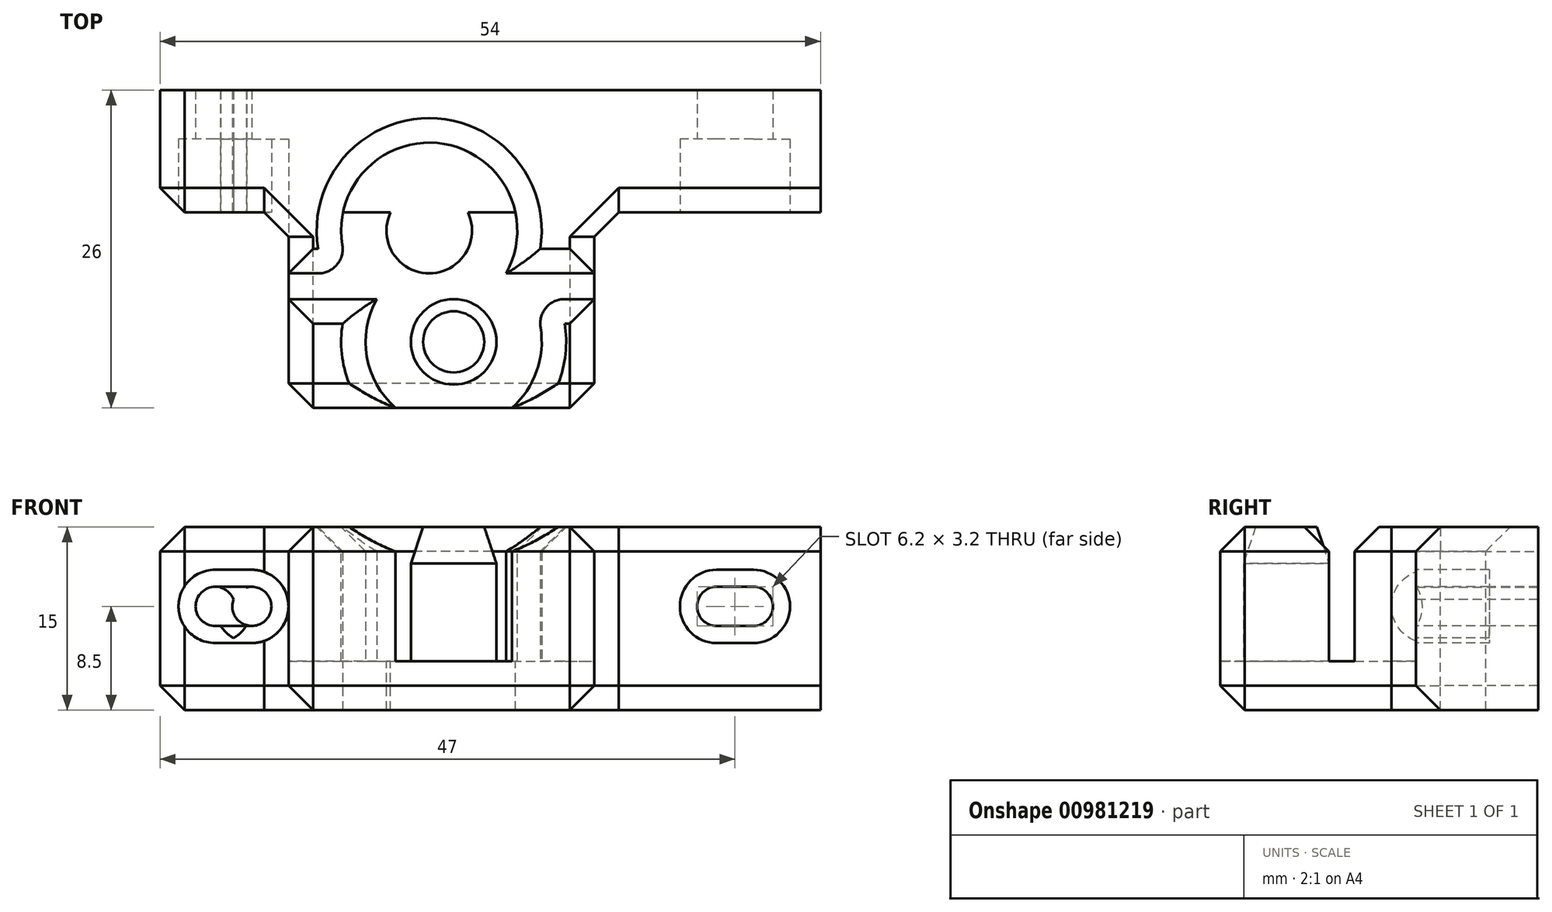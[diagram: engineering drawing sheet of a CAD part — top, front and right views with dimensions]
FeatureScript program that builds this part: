
annotation { "Feature Type Name" : "Feature", "Feature Type Description" : "" }
export const myFeature = defineFeature(function(context is Context, id is Id, definition is map)
    precondition{}
    {
        {
            var Q0;
            Q0=qCreatedBy(makeId("Top.planeOp"),FACE);
            var sketch = newSketch(context, id + "F0", { "sketchPlane" : qUnion([Q0])});
            skLineSegment(sketch, "E0.bottom", {"start": v(0, 0) * mm, "end": v(54, 0) * mm});
            skLineSegment(sketch, "E0.top", {"start": v(0, 10) * mm, "end": v(54, 10) * mm});
            skLineSegment(sketch, "E0.left", {"start": v(0, 0) * mm, "end": v(0, 10) * mm});
            skLineSegment(sketch, "E0.right", {"start": v(54, 0) * mm, "end": v(54, 10) * mm});
            skLineSegment(sketch, "E1.bottom", {"start": v(10.5, 0) * mm, "end": v(35.5, 0) * mm});
            skLineSegment(sketch, "E1.top", {"start": v(10.5, -16) * mm, "end": v(35.5, -16) * mm});
            skLineSegment(sketch, "E1.left", {"start": v(10.5, 0) * mm, "end": v(10.5, -16) * mm});
            skLineSegment(sketch, "E1.right", {"start": v(35.5, 0) * mm, "end": v(35.5, -16) * mm});
            skLineSegment(sketch, "E2", {"start": v(10.5, -5) * mm, "end": v(12.92, -5) * mm});
            skLineSegment(sketch, "E3", {"start": v(33.08, -7.1) * mm, "end": v(35.5, -7.1) * mm});
            skCircle(sketch, "E4", {"center": v(22, -1.5) * mm, "radius": 3.5 * mm});
            skCircle(sketch, "E5", {"center": v(24, -10.6) * mm, "radius": 3.5 * mm});
            skArc(sketch, "E6", {"start": v(28.76, -16) * mm, "mid": v(30.78, -13.02) * mm, "end": v(31.1, -9.43) * mm});
            skArc(sketch, "E7", {"start": v(28.3, -5) * mm, "mid": v(23.23, 5.6) * mm, "end": v(14.9, -2.67) * mm});
            skLineSegment(sketch, "E8", {"start": v(22, -1.5) * mm, "end": v(22, -19) * mm, "construction": true});
            skLineSegment(sketch, "E9", {"start": v(22, -19) * mm, "end": v(24, -19) * mm, "construction": true});
            skLineSegment(sketch, "E10", {"start": v(24, -19) * mm, "end": v(24, -10.6) * mm, "construction": true});
            skPoint(sketch, "E11", {"position": v(23, -16) * mm});
            skPoint(sketch, "E12", {"position": v(23, -19) * mm});
            skArc(sketch, "E13.trimOffspring", {"start": v(17.7, -7.1) * mm, "mid": v(16.9, -11.82) * mm, "end": v(19.24, -16) * mm});
            skPoint(sketch, "E14.newPointA", {"position": v(35.5, -5) * mm});
            skArc(sketch, "E14.filletArc", {"start": v(12.92, -5) * mm, "mid": v(14.45, -4.3) * mm, "end": v(14.9, -2.67) * mm});
            skArc(sketch, "E15.filletArc", {"start": v(33.08, -7.1) * mm, "mid": v(31.55, -7.8) * mm, "end": v(31.1, -9.43) * mm});
            skLineSegment(sketch, "E16", {"start": v(17.7, -7.1) * mm, "end": v(10.5, -7.1) * mm});
            skLineSegment(sketch, "E17", {"start": v(28.3, -5) * mm, "end": v(35.5, -5) * mm});
            skSolve(sketch);
        }
        {
            var Q0;
            Q0=makeQuery(id+"F0.imprint","IMPRINT",FACE,{"disambiguationData":[TD([[makeQuery(id+"F0.imprint","IMPRINT",EDGE,{"derivedFrom":sQuery(id+"F0.wireOp",EDGE,"E0.top")}),-1.0]])]});
            var Q1;
            {var subQ6=sQuery(id+"F0.wireOp",EDGE,"E2");Q1=makeQuery(id+"F0.imprint","IMPRINT",FACE,{"disambiguationData":[TD([[makeQuery(id+"F0.imprint","IMPRINT",EDGE,{"derivedFrom":subQ6}),1.0]])]});}
            var Q2;
            {var subQ3=sQuery(id+"F0.wireOp",EDGE,"E13.trimOffspring");Q2=makeQuery(id+"F0.imprint","IMPRINT",FACE,{"disambiguationData":[TD([[makeQuery(id+"F0.imprint","IMPRINT",EDGE,{"derivedFrom":subQ3}),-1.0]])]});}
            var Q3;
            {var subQ1=sQuery(id+"F0.wireOp",EDGE,"E3");Q3=makeQuery(id+"F0.imprint","IMPRINT",FACE,{"disambiguationData":[TD([[makeQuery(id+"F0.imprint","IMPRINT",EDGE,{"derivedFrom":subQ1}),-1.0]])]});}
            var Q4;
            {var subQ5=sQuery(id+"F0.wireOp",EDGE,"E17");Q4=makeQuery(id+"F0.imprint","IMPRINT",FACE,{"disambiguationData":[TD([[makeQuery(id+"F0.imprint","IMPRINT",EDGE,{"derivedFrom":subQ5}),1.0]])]});}
            var Q5;
            {var subQ13=sQuery(id+"F0.wireOp",EDGE,"E2");Q5=makeQuery(id+"F0.imprint","IMPRINT",FACE,{"disambiguationData":[TD([[makeQuery(id+"F0.imprint","IMPRINT",EDGE,{"derivedFrom":subQ13}),-1.0]])]});}
            var Q6;
            {var subQ0=sQuery(id+"F0.wireOp",EDGE,"E4");var subQ1=sQuery(id+"F0.wireOp",EDGE,"E1.bottom");var subQ2=makeQuery(id+"F0.imprint","INTERSECT",VERTEX,{"disambiguationData":[OD(0.0)],"derivedFrom":[subQ1,subQ0]});Q6=makeQuery(id+"F0.imprint","IMPRINT",FACE,{"disambiguationData":[TD([[makeQuery(id+"F0.imprint","IMPRINT",EDGE,{"disambiguationData":[TD([[subQ2,-1.0]])],"derivedFrom":subQ1}),-1.0]])]});}
            var Q7;
            Q7=makeQuery(id+"F0.imprint","IMPRINT",FACE,{"disambiguationData":[TD([[makeQuery(id+"F0.imprint","IMPRINT",EDGE,{"derivedFrom":sQuery(id+"F0.wireOp",EDGE,"E5")}),1.0]])]});
            var Q8;
            {var subQ0=sQuery(id+"F0.wireOp",EDGE,"E4");var subQ1=sQuery(id+"F0.wireOp",EDGE,"E1.bottom");var subQ2=makeQuery(id+"F0.imprint","INTERSECT",VERTEX,{"disambiguationData":[OD(0.0)],"derivedFrom":[subQ1,subQ0]});Q8=makeQuery(id+"F0.imprint","IMPRINT",FACE,{"disambiguationData":[TD([[makeQuery(id+"F0.imprint","IMPRINT",EDGE,{"disambiguationData":[TD([[subQ2,-1.0]])],"derivedFrom":subQ1}),1.0]])]});}
            var Q9;
            {var subQ0=sQuery(id+"F0.wireOp",EDGE,"E7");var subQ1=sQuery(id+"F0.wireOp",EDGE,"E1.bottom");var subQ2=makeQuery(id+"F0.imprint","INTERSECT",VERTEX,{"disambiguationData":[OD(0.0)],"derivedFrom":[subQ1,subQ0]});Q9=makeQuery(id+"F0.imprint","IMPRINT",FACE,{"disambiguationData":[TD([[makeQuery(id+"F0.imprint","IMPRINT",EDGE,{"disambiguationData":[TD([[subQ2,-1.0]])],"derivedFrom":subQ1}),1.0]])]});}
            extrude(context, id + "F1", {"entities" : qUnion([Q0, Q1, Q2, Q3, Q4, Q5, Q6, Q7, Q8, Q9]), "oppositeDirection" : true, "depth" : 4 * mm, "offsetDistance" : 25 * mm});
        }
        {
            var Q0;
            Q0=makeQuery(id+"F0.imprint","IMPRINT",FACE,{"disambiguationData":[TD([[makeQuery(id+"F0.imprint","IMPRINT",EDGE,{"derivedFrom":sQuery(id+"F0.wireOp",EDGE,"E0.top")}),-1.0]])]});
            var Q1;
            {var subQ5=sQuery(id+"F0.wireOp",EDGE,"E17");Q1=makeQuery(id+"F0.imprint","IMPRINT",FACE,{"disambiguationData":[TD([[makeQuery(id+"F0.imprint","IMPRINT",EDGE,{"derivedFrom":subQ5}),1.0]])]});}
            var Q2;
            {var subQ6=sQuery(id+"F0.wireOp",EDGE,"E2");Q2=makeQuery(id+"F0.imprint","IMPRINT",FACE,{"disambiguationData":[TD([[makeQuery(id+"F0.imprint","IMPRINT",EDGE,{"derivedFrom":subQ6}),1.0]])]});}
            var Q3;
            {var subQ3=sQuery(id+"F0.wireOp",EDGE,"E13.trimOffspring");Q3=makeQuery(id+"F0.imprint","IMPRINT",FACE,{"disambiguationData":[TD([[makeQuery(id+"F0.imprint","IMPRINT",EDGE,{"derivedFrom":subQ3}),-1.0]])]});}
            var Q4;
            {var subQ1=sQuery(id+"F0.wireOp",EDGE,"E3");Q4=makeQuery(id+"F0.imprint","IMPRINT",FACE,{"disambiguationData":[TD([[makeQuery(id+"F0.imprint","IMPRINT",EDGE,{"derivedFrom":subQ1}),-1.0]])]});}
            var Q5;
            Q5=makeQuery(id+"F0.imprint","IMPRINT",FACE,{"disambiguationData":[TD([[makeQuery(id+"F0.imprint","IMPRINT",EDGE,{"derivedFrom":sQuery(id+"F0.wireOp",EDGE,"E5")}),1.0]])]});
            var Q6;
            {var subQ0=sQuery(id+"F0.wireOp",EDGE,"E4");var subQ1=sQuery(id+"F0.wireOp",EDGE,"E1.bottom");var subQ2=makeQuery(id+"F0.imprint","INTERSECT",VERTEX,{"disambiguationData":[OD(0.0)],"derivedFrom":[subQ1,subQ0]});Q6=makeQuery(id+"F0.imprint","IMPRINT",FACE,{"disambiguationData":[TD([[makeQuery(id+"F0.imprint","IMPRINT",EDGE,{"disambiguationData":[TD([[subQ2,-1.0]])],"derivedFrom":subQ1}),-1.0]])]});}
            var Q7;
            {var subQ0=sQuery(id+"F0.wireOp",EDGE,"E4");var subQ1=sQuery(id+"F0.wireOp",EDGE,"E1.bottom");var subQ2=makeQuery(id+"F0.imprint","INTERSECT",VERTEX,{"disambiguationData":[OD(0.0)],"derivedFrom":[subQ1,subQ0]});Q7=makeQuery(id+"F0.imprint","IMPRINT",FACE,{"disambiguationData":[TD([[makeQuery(id+"F0.imprint","IMPRINT",EDGE,{"disambiguationData":[TD([[subQ2,-1.0]])],"derivedFrom":subQ1}),1.0]])]});}
            extrude(context, id + "F2", {"entities" : qUnion([Q0, Q1, Q2, Q3, Q4, Q5, Q6, Q7]), "operationType" : NewBodyOperationType.ADD, "depth" : 11 * mm, "offsetDistance" : 25 * mm});
        }
        {
            var Q0;
            Q0=makeQuery(id+"F2.opExtrude","CAP_EDGE",EDGE,{"disambiguationData":[OSD([sQuery(id+"F0.wireOp",EDGE,"E2")])],"isStart":false});
            var Q1;
            Q1=makeQuery(id+"F2.opExtrude","CAP_EDGE",EDGE,{"disambiguationData":[OSD([sQuery(id+"F0.wireOp",EDGE,"E17")])],"isStart":false});
            var Q2;
            Q2=makeQuery(id+"F2.opExtrude","CAP_EDGE",EDGE,{"disambiguationData":[OSD([sQuery(id+"F0.wireOp",EDGE,"E3")])],"isStart":false});
            var Q3;
            Q3=makeQuery(id+"F2.opExtrude","CAP_EDGE",EDGE,{"disambiguationData":[OSD([sQuery(id+"F0.wireOp",EDGE,"E13.trimOffspring")])],"isStart":false});
            var Q4;
            Q4=makeQuery(id+"F2.opExtrude","CAP_EDGE",EDGE,{"disambiguationData":[OSD([sQuery(id+"F0.wireOp",EDGE,"E16")])],"isStart":false});
            chamfer(context, id + "F3", {"entities" : qUnion([Q0, Q1, Q2, Q3, Q4]), "width" : 2 * mm, "tangentPropagation" : true});
        }
        {
            var Q0;
            Q0=makeQuery(id+"F2.opExtrude","CAP_FACE",FACE,{"disambiguationData":[OSD([sQuery(id+"F0.wireOp",EDGE,"E4")])],"isStart":false});
            var Q1;
            Q1=makeQuery(id+"F2.opExtrude","CAP_EDGE",EDGE,{"disambiguationData":[OSD([sQuery(id+"F0.wireOp",EDGE,"E5")])],"isStart":false});
            chamfer(context, id + "F4", {"entities" : qUnion([Q0, Q1]), "chamferType" : ChamferType.TWO_OFFSETS, "width1" : 1 * mm, "oppositeDirection" : false, "width2" : 3 * mm, "tangentPropagation" : true});
        }
        {
            var Q0;
            {var subQ0=sQuery(id+"F0.wireOp",EDGE,"E0.bottom");var subQ1=makeQuery(id+"F0.imprint","IMPRINT",EDGE,{"disambiguationData":[TD([[makeQuery(id+"F0.imprint","INTERSECT",VERTEX,{"derivedFrom":[subQ0,sQuery(id+"F0.wireOp",EDGE,"E0.right")]}),1.0]])],"derivedFrom":subQ0});Q0=makeQuery(id+"F2.boolean.opBoolean","MERGE",FACE,{"derivedFrom":[makeQuery(id+"F1.opExtrude","SWEPT_FACE",FACE,{"disambiguationData":[OSD([subQ0]),TDD([subQ1])]}),makeQuery(id+"F2.opExtrude","SWEPT_FACE",FACE,{"disambiguationData":[OSD([subQ0]),TDD([subQ1])]})]});}
            var sketch = newSketch(context, id + "F5", { "sketchPlane" : qUnion([Q0])});
            skCircle(sketch, "E18", {"center": v(4.5, 4.5) * mm, "radius": 1.6 * mm});
            skCircle(sketch, "E19", {"center": v(4.5, 4.5) * mm, "radius": 3 * mm});
            skCircle(sketch, "E20", {"center": v(48.5, 4.5) * mm, "radius": 1.6 * mm});
            skCircle(sketch, "E21", {"center": v(48.5, 4.5) * mm, "radius": 3 * mm});
            skCircle(sketch, "E22", {"center": v(7.5, 4.5) * mm, "radius": 1.6 * mm});
            skCircle(sketch, "E23", {"center": v(7.5, 4.5) * mm, "radius": 3 * mm});
            skCircle(sketch, "E24", {"center": v(45.5, 4.5) * mm, "radius": 1.6 * mm});
            skCircle(sketch, "E25", {"center": v(45.5, 4.5) * mm, "radius": 3 * mm});
            skLineSegment(sketch, "E26", {"start": v(4.5, 6.1) * mm, "end": v(7.5, 6.1) * mm});
            skLineSegment(sketch, "E27", {"start": v(7.5, 2.9) * mm, "end": v(4.5, 2.9) * mm});
            skLineSegment(sketch, "E28", {"start": v(45.5, 2.9) * mm, "end": v(48.5, 2.9) * mm});
            skLineSegment(sketch, "E29", {"start": v(48.5, 6.1) * mm, "end": v(45.5, 6.1) * mm});
            skLineSegment(sketch, "E30", {"start": v(45.5, 7.5) * mm, "end": v(48.5, 7.5) * mm});
            skLineSegment(sketch, "E31", {"start": v(48.5, 1.5) * mm, "end": v(45.5, 1.5) * mm});
            skLineSegment(sketch, "E32", {"start": v(7.5, 7.5) * mm, "end": v(4.5, 7.5) * mm});
            skLineSegment(sketch, "E33", {"start": v(4.5, 1.5) * mm, "end": v(7.5, 1.5) * mm});
            skSolve(sketch);
        }
        {
            var Q0;
            {var subQ0=sQuery(id+"F5.wireOp",EDGE,"E18");var subQ1=makeQuery(id+"F5.imprint","INTERSECT",VERTEX,{"derivedFrom":[subQ0,sQuery(id+"F5.wireOp",EDGE,"E26")]});Q0=makeQuery(id+"F5.imprint","IMPRINT",FACE,{"disambiguationData":[TD([[makeQuery(id+"F5.imprint","IMPRINT",EDGE,{"disambiguationData":[TD([[subQ1,1.0]])],"derivedFrom":subQ0}),1.0]])]});}
            var Q1;
            {var subQ0=sQuery(id+"F5.wireOp",EDGE,"E23");var subQ1=sQuery(id+"F5.wireOp",EDGE,"E18");var subQ2=makeQuery(id+"F5.imprint","INTERSECT",VERTEX,{"disambiguationData":[OD(0.0)],"derivedFrom":[subQ1,subQ0]});Q1=makeQuery(id+"F5.imprint","IMPRINT",FACE,{"disambiguationData":[TD([[makeQuery(id+"F5.imprint","IMPRINT",EDGE,{"disambiguationData":[TD([[subQ2,1.0]])],"derivedFrom":subQ1}),1.0]])]});}
            var Q2;
            {var subQ0=sQuery(id+"F5.wireOp",EDGE,"E22");var subQ1=sQuery(id+"F5.wireOp",EDGE,"E18");var subQ2=makeQuery(id+"F5.imprint","INTERSECT",VERTEX,{"disambiguationData":[OD(0.0)],"derivedFrom":[subQ1,subQ0]});Q2=makeQuery(id+"F5.imprint","IMPRINT",FACE,{"disambiguationData":[TD([[makeQuery(id+"F5.imprint","IMPRINT",EDGE,{"disambiguationData":[TD([[subQ2,1.0]])],"derivedFrom":subQ1}),-1.0]])]});}
            var Q3;
            {var subQ1=sQuery(id+"F5.wireOp",EDGE,"E18");var subQ5=sQuery(id+"F5.wireOp",EDGE,"E23");var subQ6=makeQuery(id+"F5.imprint","INTERSECT",VERTEX,{"disambiguationData":[OD(0.0)],"derivedFrom":[subQ1,subQ5]});Q3=makeQuery(id+"F5.imprint","IMPRINT",FACE,{"disambiguationData":[TD([[makeQuery(id+"F5.imprint","IMPRINT",EDGE,{"disambiguationData":[TD([[subQ6,1.0]])],"derivedFrom":subQ1}),-1.0]])]});}
            var Q4;
            {var subQ0=sQuery(id+"F5.wireOp",EDGE,"E22");var subQ1=sQuery(id+"F5.wireOp",EDGE,"E18");var subQ2=makeQuery(id+"F5.imprint","INTERSECT",VERTEX,{"disambiguationData":[OD(0.0)],"derivedFrom":[subQ1,subQ0]});Q4=makeQuery(id+"F5.imprint","IMPRINT",FACE,{"disambiguationData":[TD([[makeQuery(id+"F5.imprint","IMPRINT",EDGE,{"disambiguationData":[TD([[subQ2,1.0]])],"derivedFrom":subQ1}),1.0]])]});}
            var Q5;
            {var subQ0=sQuery(id+"F5.wireOp",EDGE,"E23");var subQ1=sQuery(id+"F5.wireOp",EDGE,"E18");var subQ2=makeQuery(id+"F5.imprint","INTERSECT",VERTEX,{"disambiguationData":[OD(1.0)],"derivedFrom":[subQ1,subQ0]});Q5=makeQuery(id+"F5.imprint","IMPRINT",FACE,{"disambiguationData":[TD([[makeQuery(id+"F5.imprint","IMPRINT",EDGE,{"disambiguationData":[TD([[subQ2,-1.0]])],"derivedFrom":subQ1}),-1.0]])]});}
            var Q6;
            {var subQ0=sQuery(id+"F5.wireOp",EDGE,"E22");var subQ1=sQuery(id+"F5.wireOp",EDGE,"E19");var subQ2=makeQuery(id+"F5.imprint","INTERSECT",VERTEX,{"disambiguationData":[OD(0.0)],"derivedFrom":[subQ1,subQ0]});Q6=makeQuery(id+"F5.imprint","IMPRINT",FACE,{"disambiguationData":[TD([[makeQuery(id+"F5.imprint","IMPRINT",EDGE,{"disambiguationData":[TD([[subQ2,1.0]])],"derivedFrom":subQ1}),-1.0]])]});}
            var Q7;
            {var subQ0=sQuery(id+"F5.wireOp",EDGE,"E27");var subQ1=sQuery(id+"F5.wireOp",EDGE,"E19");var subQ2=makeQuery(id+"F5.imprint","INTERSECT",VERTEX,{"derivedFrom":[subQ1,subQ0]});Q7=makeQuery(id+"F5.imprint","IMPRINT",FACE,{"disambiguationData":[TD([[makeQuery(id+"F5.imprint","IMPRINT",EDGE,{"disambiguationData":[TD([[subQ2,-1.0]])],"derivedFrom":subQ1}),-1.0]])]});}
            var Q8;
            {var subQ0=sQuery(id+"F5.wireOp",EDGE,"E27");var subQ1=sQuery(id+"F5.wireOp",EDGE,"E18");var subQ2=makeQuery(id+"F5.imprint","INTERSECT",VERTEX,{"derivedFrom":[subQ1,subQ0]});Q8=makeQuery(id+"F5.imprint","IMPRINT",FACE,{"disambiguationData":[TD([[makeQuery(id+"F5.imprint","IMPRINT",EDGE,{"disambiguationData":[TD([[subQ2,-1.0]])],"derivedFrom":subQ1}),-1.0]])]});}
            var Q9;
            {var subQ0=sQuery(id+"F5.wireOp",EDGE,"E26");var subQ1=sQuery(id+"F5.wireOp",EDGE,"E18");var subQ2=makeQuery(id+"F5.imprint","INTERSECT",VERTEX,{"derivedFrom":[subQ1,subQ0]});Q9=makeQuery(id+"F5.imprint","IMPRINT",FACE,{"disambiguationData":[TD([[makeQuery(id+"F5.imprint","IMPRINT",EDGE,{"disambiguationData":[TD([[subQ2,1.0]])],"derivedFrom":subQ1}),-1.0]])]});}
            var Q10;
            {var subQ0=sQuery(id+"F5.wireOp",EDGE,"E26");var subQ1=sQuery(id+"F5.wireOp",EDGE,"E19");var subQ2=makeQuery(id+"F5.imprint","INTERSECT",VERTEX,{"derivedFrom":[subQ1,subQ0]});Q10=makeQuery(id+"F5.imprint","IMPRINT",FACE,{"disambiguationData":[TD([[makeQuery(id+"F5.imprint","IMPRINT",EDGE,{"disambiguationData":[TD([[subQ2,1.0]])],"derivedFrom":subQ1}),-1.0]])]});}
            var Q11;
            {var subQ0=sQuery(id+"F5.wireOp",EDGE,"E24");var subQ1=sQuery(id+"F5.wireOp",EDGE,"E20");var subQ2=makeQuery(id+"F5.imprint","INTERSECT",VERTEX,{"disambiguationData":[OD(0.0)],"derivedFrom":[subQ1,subQ0]});Q11=makeQuery(id+"F5.imprint","IMPRINT",FACE,{"disambiguationData":[TD([[makeQuery(id+"F5.imprint","IMPRINT",EDGE,{"disambiguationData":[TD([[subQ2,-1.0]])],"derivedFrom":subQ1}),1.0]])]});}
            var Q12;
            {var subQ0=sQuery(id+"F5.wireOp",EDGE,"E25");var subQ1=sQuery(id+"F5.wireOp",EDGE,"E20");var subQ2=makeQuery(id+"F5.imprint","INTERSECT",VERTEX,{"disambiguationData":[OD(0.0)],"derivedFrom":[subQ1,subQ0]});Q12=makeQuery(id+"F5.imprint","IMPRINT",FACE,{"disambiguationData":[TD([[makeQuery(id+"F5.imprint","IMPRINT",EDGE,{"disambiguationData":[TD([[subQ2,-1.0]])],"derivedFrom":subQ1}),1.0]])]});}
            var Q13;
            {var subQ0=sQuery(id+"F5.wireOp",EDGE,"E25");var subQ1=sQuery(id+"F5.wireOp",EDGE,"E20");var subQ2=makeQuery(id+"F5.imprint","INTERSECT",VERTEX,{"disambiguationData":[OD(0.0)],"derivedFrom":[subQ1,subQ0]});Q13=makeQuery(id+"F5.imprint","IMPRINT",FACE,{"disambiguationData":[TD([[makeQuery(id+"F5.imprint","IMPRINT",EDGE,{"disambiguationData":[TD([[subQ2,-1.0]])],"derivedFrom":subQ1}),-1.0]])]});}
            var Q14;
            {var subQ0=sQuery(id+"F5.wireOp",EDGE,"E24");var subQ1=sQuery(id+"F5.wireOp",EDGE,"E20");var subQ2=makeQuery(id+"F5.imprint","INTERSECT",VERTEX,{"disambiguationData":[OD(0.0)],"derivedFrom":[subQ1,subQ0]});Q14=makeQuery(id+"F5.imprint","IMPRINT",FACE,{"disambiguationData":[TD([[makeQuery(id+"F5.imprint","IMPRINT",EDGE,{"disambiguationData":[TD([[subQ2,-1.0]])],"derivedFrom":subQ1}),-1.0]])]});}
            var Q15;
            {var subQ0=sQuery(id+"F5.wireOp",EDGE,"E24");var subQ1=sQuery(id+"F5.wireOp",EDGE,"E20");var subQ2=makeQuery(id+"F5.imprint","INTERSECT",VERTEX,{"disambiguationData":[OD(1.0)],"derivedFrom":[subQ1,subQ0]});Q15=makeQuery(id+"F5.imprint","IMPRINT",FACE,{"disambiguationData":[TD([[makeQuery(id+"F5.imprint","IMPRINT",EDGE,{"disambiguationData":[TD([[subQ2,-1.0]])],"derivedFrom":subQ1}),-1.0]])]});}
            var Q16;
            {var subQ0=sQuery(id+"F5.wireOp",EDGE,"E24");var subQ1=sQuery(id+"F5.wireOp",EDGE,"E21");var subQ2=makeQuery(id+"F5.imprint","INTERSECT",VERTEX,{"disambiguationData":[OD(0.0)],"derivedFrom":[subQ1,subQ0]});Q16=makeQuery(id+"F5.imprint","IMPRINT",FACE,{"disambiguationData":[TD([[makeQuery(id+"F5.imprint","IMPRINT",EDGE,{"disambiguationData":[TD([[subQ2,-1.0]])],"derivedFrom":subQ1}),-1.0]])]});}
            var Q17;
            {var subQ0=sQuery(id+"F5.wireOp",EDGE,"E20");var subQ1=makeQuery(id+"F5.imprint","INTERSECT",VERTEX,{"derivedFrom":[subQ0,sQuery(id+"F5.wireOp",EDGE,"E29")]});Q17=makeQuery(id+"F5.imprint","IMPRINT",FACE,{"disambiguationData":[TD([[makeQuery(id+"F5.imprint","IMPRINT",EDGE,{"disambiguationData":[TD([[subQ1,-1.0]])],"derivedFrom":subQ0}),1.0]])]});}
            var Q18;
            {var subQ0=sQuery(id+"F5.wireOp",EDGE,"E28");var subQ1=sQuery(id+"F5.wireOp",EDGE,"E20");var subQ2=makeQuery(id+"F5.imprint","INTERSECT",VERTEX,{"derivedFrom":[subQ1,subQ0]});Q18=makeQuery(id+"F5.imprint","IMPRINT",FACE,{"disambiguationData":[TD([[makeQuery(id+"F5.imprint","IMPRINT",EDGE,{"disambiguationData":[TD([[subQ2,1.0]])],"derivedFrom":subQ1}),-1.0]])]});}
            var Q19;
            {var subQ0=sQuery(id+"F5.wireOp",EDGE,"E24");var subQ1=sQuery(id+"F5.wireOp",EDGE,"E21");var subQ2=makeQuery(id+"F5.imprint","INTERSECT",VERTEX,{"disambiguationData":[OD(1.0)],"derivedFrom":[subQ1,subQ0]});Q19=makeQuery(id+"F5.imprint","IMPRINT",FACE,{"disambiguationData":[TD([[makeQuery(id+"F5.imprint","IMPRINT",EDGE,{"disambiguationData":[TD([[subQ2,-1.0]])],"derivedFrom":subQ1}),-1.0]])]});}
            var Q20;
            {var subQ0=sQuery(id+"F5.wireOp",EDGE,"E29");var subQ1=sQuery(id+"F5.wireOp",EDGE,"E21");var subQ2=makeQuery(id+"F5.imprint","INTERSECT",VERTEX,{"derivedFrom":[subQ1,subQ0]});Q20=makeQuery(id+"F5.imprint","IMPRINT",FACE,{"disambiguationData":[TD([[makeQuery(id+"F5.imprint","IMPRINT",EDGE,{"disambiguationData":[TD([[subQ2,-1.0]])],"derivedFrom":subQ1}),-1.0]])]});}
            var Q21;
            {var subQ0=sQuery(id+"F5.wireOp",EDGE,"E29");var subQ1=sQuery(id+"F5.wireOp",EDGE,"E20");var subQ2=makeQuery(id+"F5.imprint","INTERSECT",VERTEX,{"derivedFrom":[subQ1,subQ0]});Q21=makeQuery(id+"F5.imprint","IMPRINT",FACE,{"disambiguationData":[TD([[makeQuery(id+"F5.imprint","IMPRINT",EDGE,{"disambiguationData":[TD([[subQ2,-1.0]])],"derivedFrom":subQ1}),-1.0]])]});}
            extrude(context, id + "F6", {"entities" : qUnion([Q0, Q1, Q2, Q3, Q4, Q5, Q6, Q7, Q8, Q9, Q10, Q11, Q12, Q13, Q14, Q15, Q16, Q17, Q18, Q19, Q20, Q21]), "operationType" : NewBodyOperationType.REMOVE, "endBound" : BoundingType.THROUGH_ALL, "oppositeDirection" : true, "depth" : 25 * mm, "offsetDistance" : 25 * mm});
        }
        {
            var Q0;
            {var subQ6=sQuery(id+"F5.wireOp",EDGE,"E26");var subQ7=sQuery(id+"F5.wireOp",EDGE,"E18");var subQ8=makeQuery(id+"F5.imprint","INTERSECT",VERTEX,{"derivedFrom":[subQ7,subQ6]});Q0=makeQuery(id+"F5.imprint","IMPRINT",FACE,{"disambiguationData":[TD([[makeQuery(id+"F5.imprint","IMPRINT",EDGE,{"disambiguationData":[TD([[subQ8,-1.0]])],"derivedFrom":subQ7}),-1.0]])]});}
            var Q1;
            {var subQ2=sQuery(id+"F5.wireOp",EDGE,"E19");var subQ4=sQuery(id+"F5.wireOp",EDGE,"E26");var subQ11=makeQuery(id+"F5.imprint","INTERSECT",VERTEX,{"derivedFrom":[subQ2,subQ4]});Q1=makeQuery(id+"F5.imprint","IMPRINT",FACE,{"disambiguationData":[TD([[makeQuery(id+"F5.imprint","IMPRINT",EDGE,{"disambiguationData":[TD([[subQ11,-1.0]])],"derivedFrom":subQ2}),-1.0]])]});}
            var Q2;
            {var subQ0=sQuery(id+"F5.wireOp",EDGE,"E26");var subQ1=sQuery(id+"F5.wireOp",EDGE,"E19");var subQ2=makeQuery(id+"F5.imprint","INTERSECT",VERTEX,{"derivedFrom":[subQ1,subQ0]});Q2=makeQuery(id+"F5.imprint","IMPRINT",FACE,{"disambiguationData":[TD([[makeQuery(id+"F5.imprint","IMPRINT",EDGE,{"disambiguationData":[TD([[subQ2,-1.0]])],"derivedFrom":subQ1}),1.0]])]});}
            var Q3;
            {var subQ0=sQuery(id+"F5.wireOp",EDGE,"E23");var subQ1=sQuery(id+"F5.wireOp",EDGE,"E19");var subQ2=makeQuery(id+"F5.imprint","INTERSECT",VERTEX,{"disambiguationData":[OD(1.0)],"derivedFrom":[subQ1,subQ0]});Q3=makeQuery(id+"F5.imprint","IMPRINT",FACE,{"disambiguationData":[TD([[makeQuery(id+"F5.imprint","IMPRINT",EDGE,{"disambiguationData":[TD([[subQ2,-1.0]])],"derivedFrom":subQ1}),1.0]])]});}
            var Q4;
            {var subQ0=sQuery(id+"F5.wireOp",EDGE,"E33");Q4=makeQuery(id+"F5.imprint","IMPRINT",FACE,{"disambiguationData":[TD([[makeQuery(id+"F5.imprint","IMPRINT",EDGE,{"derivedFrom":subQ0}),1.0]])]});}
            var Q5;
            {var subQ0=sQuery(id+"F5.wireOp",EDGE,"E32");Q5=makeQuery(id+"F5.imprint","IMPRINT",FACE,{"disambiguationData":[TD([[makeQuery(id+"F5.imprint","IMPRINT",EDGE,{"derivedFrom":subQ0}),1.0]])]});}
            var Q6;
            {var subQ0=sQuery(id+"F5.wireOp",EDGE,"E28");var subQ1=sQuery(id+"F5.wireOp",EDGE,"E21");var subQ2=makeQuery(id+"F5.imprint","INTERSECT",VERTEX,{"derivedFrom":[subQ1,subQ0]});Q6=makeQuery(id+"F5.imprint","IMPRINT",FACE,{"disambiguationData":[TD([[makeQuery(id+"F5.imprint","IMPRINT",EDGE,{"disambiguationData":[TD([[subQ2,-1.0]])],"derivedFrom":subQ1}),1.0]])]});}
            var Q7;
            {var subQ0=sQuery(id+"F5.wireOp",EDGE,"E25");var subQ1=sQuery(id+"F5.wireOp",EDGE,"E21");var subQ2=makeQuery(id+"F5.imprint","INTERSECT",VERTEX,{"disambiguationData":[OD(0.0)],"derivedFrom":[subQ1,subQ0]});Q7=makeQuery(id+"F5.imprint","IMPRINT",FACE,{"disambiguationData":[TD([[makeQuery(id+"F5.imprint","IMPRINT",EDGE,{"disambiguationData":[TD([[subQ2,-1.0]])],"derivedFrom":subQ1}),1.0]])]});}
            var Q8;
            {var subQ0=sQuery(id+"F5.wireOp",EDGE,"E30");Q8=makeQuery(id+"F5.imprint","IMPRINT",FACE,{"disambiguationData":[TD([[makeQuery(id+"F5.imprint","IMPRINT",EDGE,{"derivedFrom":subQ0}),-1.0]])]});}
            var Q9;
            {var subQ0=sQuery(id+"F5.wireOp",EDGE,"E31");Q9=makeQuery(id+"F5.imprint","IMPRINT",FACE,{"disambiguationData":[TD([[makeQuery(id+"F5.imprint","IMPRINT",EDGE,{"derivedFrom":subQ0}),-1.0]])]});}
            var Q10;
            {var subQ8=sQuery(id+"F5.wireOp",EDGE,"E28");var subQ10=sQuery(id+"F5.wireOp",EDGE,"E20");var subQ11=makeQuery(id+"F5.imprint","INTERSECT",VERTEX,{"derivedFrom":[subQ10,subQ8]});Q10=makeQuery(id+"F5.imprint","IMPRINT",FACE,{"disambiguationData":[TD([[makeQuery(id+"F5.imprint","IMPRINT",EDGE,{"disambiguationData":[TD([[subQ11,-1.0]])],"derivedFrom":subQ10}),-1.0]])]});}
            var Q11;
            {var subQ5=sQuery(id+"F5.wireOp",EDGE,"E25");var subQ7=sQuery(id+"F5.wireOp",EDGE,"E21");var subQ8=makeQuery(id+"F5.imprint","INTERSECT",VERTEX,{"disambiguationData":[OD(0.0)],"derivedFrom":[subQ7,subQ5]});Q11=makeQuery(id+"F5.imprint","IMPRINT",FACE,{"disambiguationData":[TD([[makeQuery(id+"F5.imprint","IMPRINT",EDGE,{"disambiguationData":[TD([[subQ8,-1.0]])],"derivedFrom":subQ7}),-1.0]])]});}
            extrude(context, id + "F7", {"entities" : qUnion([Q0, Q1, Q2, Q3, Q4, Q5, Q6, Q7, Q8, Q9, Q10, Q11]), "operationType" : NewBodyOperationType.REMOVE, "oppositeDirection" : true, "depth" : 6 * mm, "offsetDistance" : 25 * mm});
        }
        {
            var Q0;
            {var subQ0=sQuery(id+"F0.wireOp",EDGE,"E1.left");var subQ1=sQuery(id+"F0.wireOp",EDGE,"E1.top");Q0=makeQuery(id+"F2.boolean.opBoolean","MERGE",EDGE,{"derivedFrom":[makeQuery(id+"F1.opExtrude","SWEPT_EDGE",EDGE,{"disambiguationData":[OSD([subQ1,subQ0])]}),makeQuery(id+"F2.opExtrude","SWEPT_EDGE",EDGE,{"disambiguationData":[OSD([subQ1,subQ0])]})]});}
            var Q1;
            {var subQ0=sQuery(id+"F0.wireOp",EDGE,"E1.right");var subQ1=sQuery(id+"F0.wireOp",EDGE,"E1.top");Q1=makeQuery(id+"F2.boolean.opBoolean","MERGE",EDGE,{"derivedFrom":[makeQuery(id+"F1.opExtrude","SWEPT_EDGE",EDGE,{"disambiguationData":[OSD([subQ1,subQ0])]}),makeQuery(id+"F2.opExtrude","SWEPT_EDGE",EDGE,{"disambiguationData":[OSD([subQ1,subQ0])]})]});}
            var Q2;
            {var subQ0=sQuery(id+"F0.wireOp",EDGE,"E1.right");var subQ1=sQuery(id+"F0.wireOp",EDGE,"E1.bottom");var subQ2=sQuery(id+"F0.wireOp",EDGE,"E0.bottom");Q2=makeQuery(id+"F2.boolean.opBoolean","MERGE",EDGE,{"derivedFrom":[makeQuery(id+"F1.opExtrude","SWEPT_EDGE",EDGE,{"disambiguationData":[OSD([subQ2,subQ1,subQ0])]}),makeQuery(id+"F2.opExtrude","SWEPT_EDGE",EDGE,{"disambiguationData":[OSD([subQ2,subQ1,subQ0])]})]});}
            var Q3;
            {var subQ0=sQuery(id+"F0.wireOp",EDGE,"E0.left");var subQ1=sQuery(id+"F0.wireOp",EDGE,"E0.bottom");var subQ2=sQuery(id+"F0.wireOp",EDGE,"E1.left");var subQ3=sQuery(id+"F0.wireOp",EDGE,"E1.bottom");var subQ6=sQuery(id+"F0.wireOp",EDGE,"E2");Q3=makeQuery(id+"F7.boolean.opBoolean","SPLIT",EDGE,{"disambiguationData":[TD([makeQuery(id+"F2.opExtrude","CAP_FACE",FACE,{"disambiguationData":[OSD([subQ1,sQuery(id+"F0.wireOp",EDGE,"E0.top"),subQ0,sQuery(id+"F0.wireOp",EDGE,"E0.right"),subQ2,sQuery(id+"F0.wireOp",EDGE,"E1.right"),subQ6,sQuery(id+"F0.wireOp",EDGE,"E7"),sQuery(id+"F0.wireOp",EDGE,"E14.filletArc"),sQuery(id+"F0.wireOp",EDGE,"E17")])],"isStart":false})])],"derivedFrom":makeQuery(id+"F2.boolean.opBoolean","MERGE",EDGE,{"derivedFrom":[makeQuery(id+"F1.opExtrude","SWEPT_EDGE",EDGE,{"disambiguationData":[OSD([subQ1,subQ3,subQ2])]}),makeQuery(id+"F2.opExtrude","SWEPT_EDGE",EDGE,{"disambiguationData":[OSD([subQ1,subQ3,subQ2])]})]})});}
            var Q4;
            {var subQ0=sQuery(id+"F0.wireOp",EDGE,"E0.left");var subQ1=sQuery(id+"F0.wireOp",EDGE,"E0.bottom");Q4=makeQuery(id+"F2.boolean.opBoolean","MERGE",EDGE,{"derivedFrom":[makeQuery(id+"F1.opExtrude","SWEPT_EDGE",EDGE,{"disambiguationData":[OSD([subQ1,subQ0])]}),makeQuery(id+"F2.opExtrude","SWEPT_EDGE",EDGE,{"disambiguationData":[OSD([subQ1,subQ0])]})]});}
            var Q5;
            {var subQ0=sQuery(id+"F0.wireOp",EDGE,"E0.bottom");Q5=makeQuery(id+"F2.opExtrude","CAP_EDGE",EDGE,{"disambiguationData":[OSD([subQ0]),TDD([makeQuery(id+"F0.imprint","IMPRINT",EDGE,{"disambiguationData":[TD([[makeQuery(id+"F0.imprint","INTERSECT",VERTEX,{"derivedFrom":[subQ0,sQuery(id+"F0.wireOp",EDGE,"E0.right")]}),1.0]])],"derivedFrom":subQ0})])],"isStart":false});}
            var Q6;
            {var subQ0=sQuery(id+"F0.wireOp",EDGE,"E0.bottom");Q6=makeQuery(id+"F1.opExtrude","CAP_EDGE",EDGE,{"disambiguationData":[OSD([subQ0]),TDD([makeQuery(id+"F0.imprint","IMPRINT",EDGE,{"disambiguationData":[TD([[makeQuery(id+"F0.imprint","INTERSECT",VERTEX,{"derivedFrom":[subQ0,sQuery(id+"F0.wireOp",EDGE,"E0.right")]}),1.0]])],"derivedFrom":subQ0})])],"isStart":false});}
            var Q7;
            Q7=makeQuery(id+"F1.opExtrude","CAP_EDGE",EDGE,{"disambiguationData":[OSD([sQuery(id+"F0.wireOp",EDGE,"E1.top")])],"isStart":false});
            var Q8;
            Q8=makeQuery(id+"F1.opExtrude","CAP_EDGE",EDGE,{"disambiguationData":[OSD([sQuery(id+"F0.wireOp",EDGE,"E1.left")])],"isStart":false});
            var Q9;
            Q9=makeQuery(id+"F1.opExtrude","CAP_EDGE",EDGE,{"disambiguationData":[OSD([sQuery(id+"F0.wireOp",EDGE,"E0.left")])],"isStart":false});
            var Q10;
            Q10=makeQuery(id+"F2.opExtrude","CAP_EDGE",EDGE,{"disambiguationData":[OSD([sQuery(id+"F0.wireOp",EDGE,"E0.left")])],"isStart":false});
            var Q11;
            {var subQ0=sQuery(id+"F0.wireOp",EDGE,"E0.bottom");Q11=makeQuery(id+"F2.opExtrude","CAP_EDGE",EDGE,{"disambiguationData":[OSD([subQ0]),TDD([makeQuery(id+"F0.imprint","IMPRINT",EDGE,{"disambiguationData":[TD([[makeQuery(id+"F0.imprint","INTERSECT",VERTEX,{"derivedFrom":[subQ0,sQuery(id+"F0.wireOp",EDGE,"E0.left")]}),-1.0]])],"derivedFrom":subQ0})])],"isStart":false});}
            var Q12;
            {var subQ0=sQuery(id+"F0.wireOp",EDGE,"E1.left");Q12=makeQuery(id+"F2.opExtrude","CAP_EDGE",EDGE,{"disambiguationData":[OSD([subQ0]),TDD([makeQuery(id+"F0.imprint","IMPRINT",EDGE,{"disambiguationData":[TD([[makeQuery(id+"F0.imprint","INTERSECT",VERTEX,{"derivedFrom":[sQuery(id+"F0.wireOp",EDGE,"E1.top"),subQ0]}),1.0]])],"derivedFrom":subQ0})])],"isStart":false});}
            var Q13;
            {var subQ0=sQuery(id+"F0.wireOp",EDGE,"E1.top");Q13=makeQuery(id+"F2.opExtrude","CAP_EDGE",EDGE,{"disambiguationData":[OSD([subQ0]),TDD([makeQuery(id+"F0.imprint","IMPRINT",EDGE,{"disambiguationData":[TD([[makeQuery(id+"F0.imprint","INTERSECT",VERTEX,{"derivedFrom":[subQ0,sQuery(id+"F0.wireOp",EDGE,"E1.left")]}),-1.0]])],"derivedFrom":subQ0})])],"isStart":false});}
            var Q14;
            {var subQ0=sQuery(id+"F0.wireOp",EDGE,"E1.top");Q14=makeQuery(id+"F2.opExtrude","CAP_EDGE",EDGE,{"disambiguationData":[OSD([subQ0]),TDD([makeQuery(id+"F0.imprint","IMPRINT",EDGE,{"disambiguationData":[TD([[makeQuery(id+"F0.imprint","INTERSECT",VERTEX,{"derivedFrom":[subQ0,sQuery(id+"F0.wireOp",EDGE,"E1.right")]}),1.0]])],"derivedFrom":subQ0})])],"isStart":false});}
            var Q15;
            {var subQ0=sQuery(id+"F0.wireOp",EDGE,"E1.right");Q15=makeQuery(id+"F2.opExtrude","CAP_EDGE",EDGE,{"disambiguationData":[OSD([subQ0]),TDD([makeQuery(id+"F0.imprint","IMPRINT",EDGE,{"disambiguationData":[TD([[makeQuery(id+"F0.imprint","INTERSECT",VERTEX,{"derivedFrom":[sQuery(id+"F0.wireOp",EDGE,"E1.top"),subQ0]}),1.0]])],"derivedFrom":subQ0})])],"isStart":false});}
            chamfer(context, id + "F8", {"entities" : qUnion([Q0, Q1, Q2, Q3, Q4, Q5, Q6, Q7, Q8, Q9, Q10, Q11, Q12, Q13, Q14, Q15]), "width" : 2 * mm, "tangentPropagation" : true});
        }
    });
